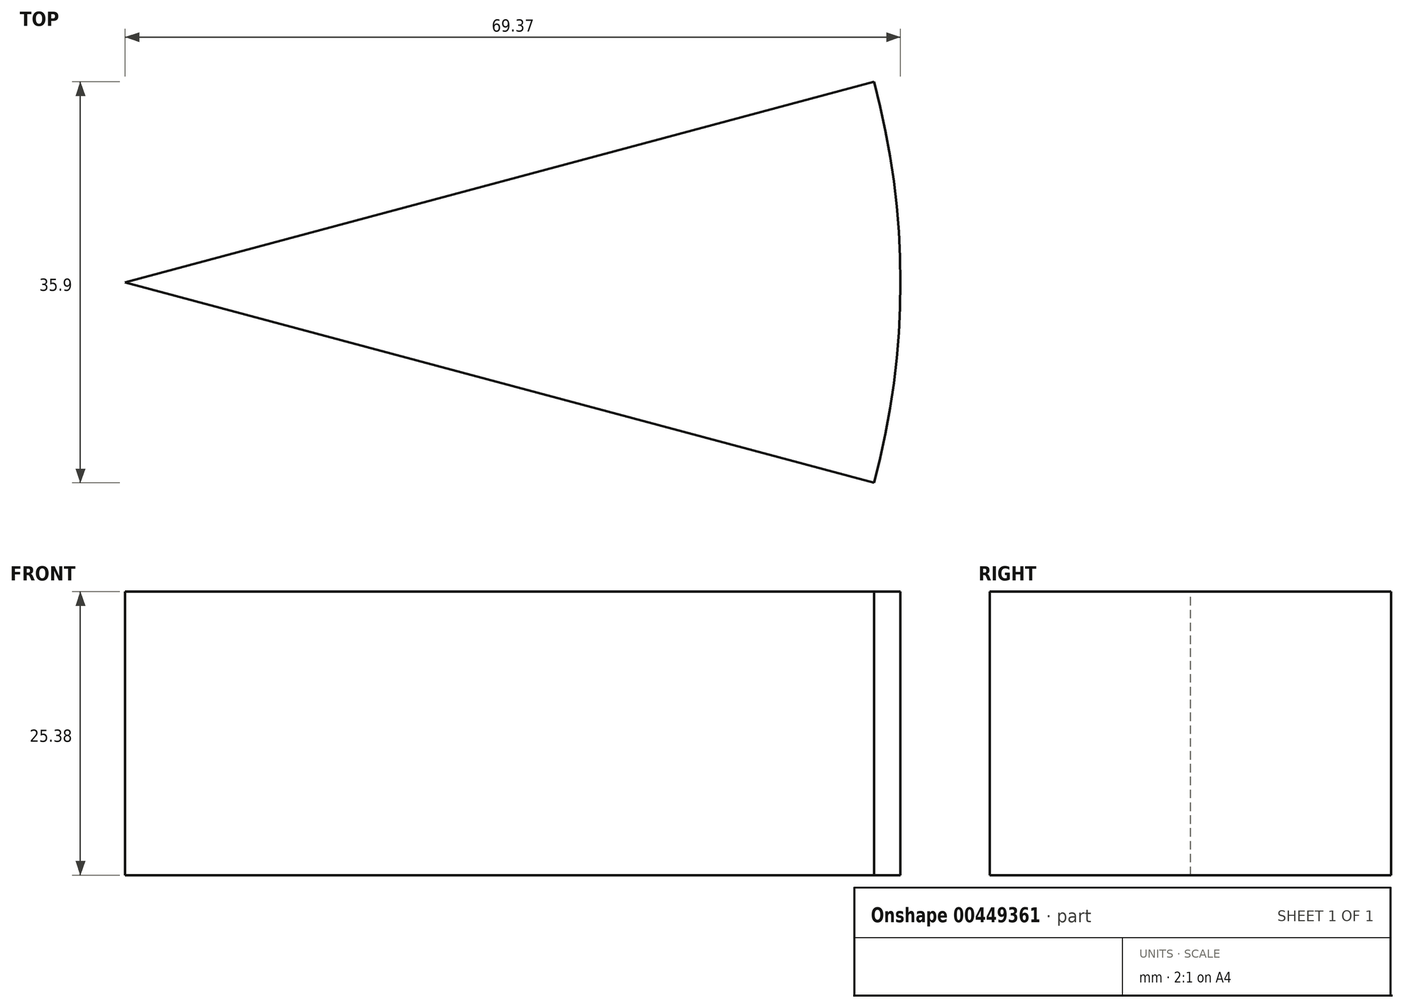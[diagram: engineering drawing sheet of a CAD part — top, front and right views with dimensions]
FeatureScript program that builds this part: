
annotation { "Feature Type Name" : "Feature", "Feature Type Description" : "" }
export const myFeature = defineFeature(function(context is Context, id is Id, definition is map)
    precondition{}
    {
        {
            var Q0;
            Q0=qCreatedBy(makeId("Front.planeOp"),FACE);
            var sketch = newSketch(context, id + "F0", { "sketchPlane" : qUnion([Q0])});
            skLineSegment(sketch, "E0.bottom", {"start": v(0, 0) * mm, "end": v(69.37, 0) * mm});
            skLineSegment(sketch, "E0.top", {"start": v(0, 25.38) * mm, "end": v(69.37, 25.38) * mm});
            skLineSegment(sketch, "E0.left", {"start": v(0, 0) * mm, "end": v(0, 25.38) * mm});
            skLineSegment(sketch, "E0.right", {"start": v(69.37, 0) * mm, "end": v(69.37, 25.38) * mm});
            skSolve(sketch);
        }
        {
            var Q0;
            Q0=makeQuery(id+"F0.imprint","IMPRINT",FACE,{"disambiguationData":[TD([[makeQuery(id+"F0.imprint","IMPRINT",EDGE,{"derivedFrom":sQuery(id+"F0.wireOp",EDGE,"E0.bottom")}),1.0]])]});
            var Q1;
            Q1=sQuery(id+"F0.wireOp",EDGE,"E0.left");
            revolve(context, id + "F1", {"entities" : qUnion([Q0]), "axis" : qUnion([Q1]), "revolveType" : RevolveType.SYMMETRIC, "angle" : 30 * degree});
        }
    });
